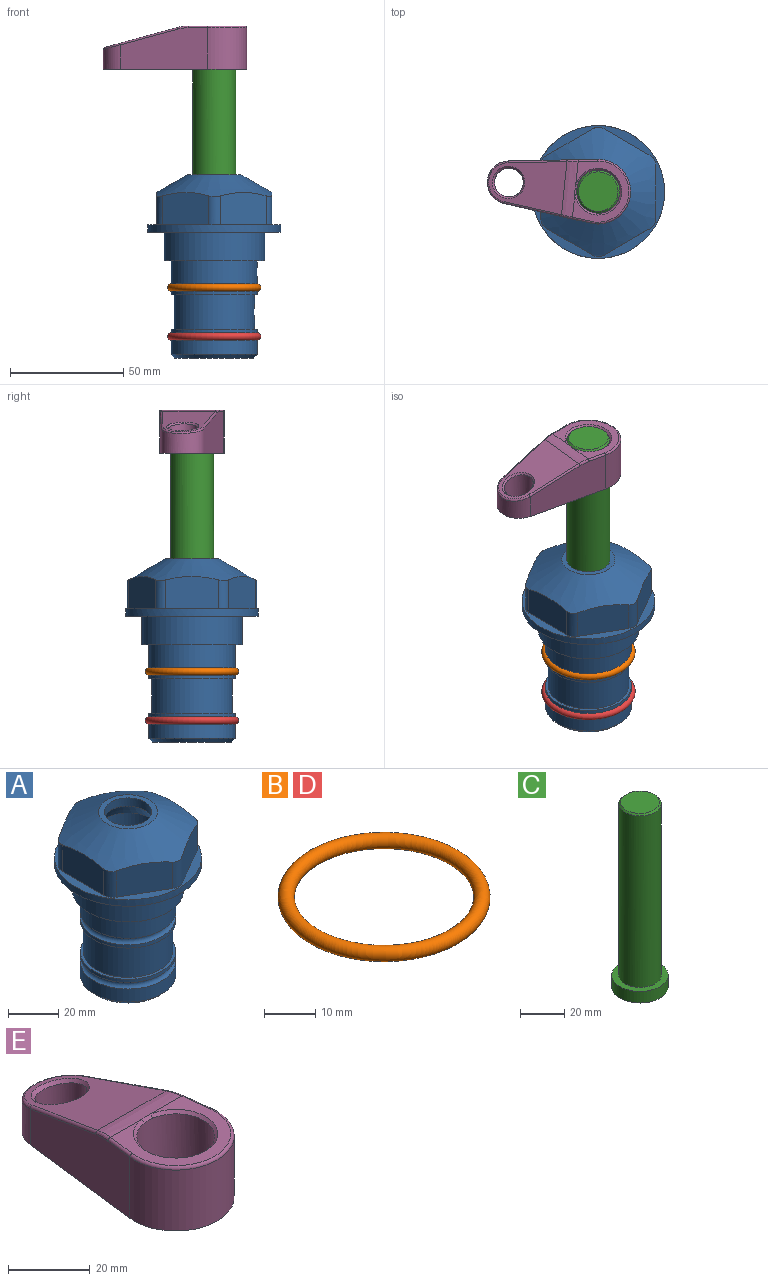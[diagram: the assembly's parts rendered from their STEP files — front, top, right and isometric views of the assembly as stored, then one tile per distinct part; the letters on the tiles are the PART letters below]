
ASSEMBLY  parts=5 mates=4
PART A: 36 faces, bbox 58.7x58.7x81 mm
  f0: cylinder r=17.78mm len=35.56mm, axis (0,0,1), area 1670.8mm2, adj f23,f24,f31
  f1: cylinder r=19.05mm len=38.1mm, axis (0,0,1), area 1191.9mm2, adj f26,f27,f30
  f2: plane 58.66x58.66mm, normal (0,0,-1), area 1150.6mm2, adj f3,f28
  f3: cylinder r=29.33mm len=58.66mm, axis (0,0,-1), area 585.1mm2, adj f2,f4
  f4: plane 58.66x58.66mm, normal (0,0,1), area 475.9mm2, adj f3,f5,f6,f7,f8,f9,f10,f11
  f5: plane 20.32x14.34mm, normal (-0.5,0.87,0), area 324.4mm2, adj f4,f15,f16,f17
  f6: plane 20.32x14.34mm, normal (0.5,0.87,0), area 324.4mm2, adj f4,f14,f15,f17
  f7: plane 23.48x14.34mm, normal (1,0,0), area 324.4mm2, adj f4,f13,f14,f17
  f8: plane 20.32x14.34mm, normal (0.5,-0.87,0), area 324.4mm2, adj f4,f12,f13,f17
  f9: plane 20.32x14.34mm, normal (-0.5,-0.87,0), area 324.4mm2, adj f4,f11,f12,f17
  f10: plane 23.48x14.34mm, normal (-1,0,0), area 324.4mm2, adj f4,f11,f16,f17
  f11: cylinder r=5.08mm len=12.85mm, axis (0,0,-1), area 67.2mm2, adj f4,f9,f10,f17
  f12: cylinder r=5.08mm len=12.85mm, axis (0,0,-1), area 67.2mm2, adj f4,f8,f9,f17
  f13: cylinder r=5.08mm len=12.85mm, axis (0,0,-1), area 67.2mm2, adj f4,f7,f8,f17
  f14: cylinder r=5.08mm len=12.85mm, axis (0,0,-1), area 67.2mm2, adj f4,f6,f7,f17
  f15: cylinder r=5.08mm len=12.85mm, axis (0,0,-1), area 67.2mm2, adj f4,f5,f6,f17
  f16: cylinder r=5.08mm len=12.85mm, axis (0,0,-1), area 67.2mm2, adj f4,f5,f10,f17
  f17: cone r=11.73mm half-angle=60deg, axis (0,0,-1), area 2071.8mm2, adj f5,f6,f7,f8,f9,f10,f11,f12
  f18: plane 23.46x23.46mm, normal (0,0,1), area 147.4mm2, adj f17,f35
  f19: plane 34.93x34.93mm, normal (0,0,-1), area 958mm2, adj f29
  f20: cylinder r=19.05mm len=38.1mm, axis (0,0,1), area 760.1mm2, adj f21,f29
  f21: torus R=19.05mm, axis (0,0,1), area 565.3mm2, adj f20,f22
  f22: cylinder r=19.05mm len=38.1mm, axis (0,0,1), area 190mm2, adj f21,f23
  f23: plane 38.1x38.1mm, normal (0,0,1), area 146.9mm2, adj f0,f22
  f24: plane 38.1x38.1mm, normal (0,0,-1), area 146.9mm2, adj f0,f25
  f25: cylinder r=19.05mm len=38.1mm, axis (0,0,1), area 190mm2, adj f24,f26
  f26: torus R=19.05mm, axis (0,0,1), area 565.3mm2, adj f1,f25
  f27: plane 44.45x44.45mm, normal (0,0,-1), area 411.7mm2, adj f1,f28
  f28: cylinder r=22.23mm len=44.45mm, axis (0,0,1), area 1773.5mm2, adj f2,f27
  f29: cone r=19.05mm half-angle=45deg, axis (0,0,1), area 257.5mm2, adj f19,f20
  f30: cylinder r=3.17mm len=6.75mm, axis (-1,0,0), area 128mm2, adj f1,f33
  f31: cylinder r=3.17mm len=6.35mm, axis (-1,0,0), area 102.5mm2, adj f0,f33
  f32: plane 25.4x25.4mm, normal (0,0,1), area 506.7mm2, adj f33
  f33: cylinder r=12.7mm len=66.42mm, axis (0,0,-1), area 5236.2mm2, adj f30,f31,f32,f34
  f34: cone r=9.53mm half-angle=30deg, axis (0,0,-1), area 443.4mm2, adj f33,f35
  f35: cylinder r=9.53mm len=19.05mm, axis (0,0,-1), area 240.9mm2, adj f18,f34
PART B: 1 faces, bbox 44.7x44.7x3.2 mm
  f0: torus R=19.05mm, axis (0,0,1), area 1193.9mm2
PART C: 6 faces, bbox 25.4x25.4x101.6 mm
  f0: plane 17.46x17.46mm, normal (0,0,1), area 239.5mm2, adj f5
  f1: plane 25.4x25.4mm, normal (0,0,-1), area 506.7mm2, adj f2
  f2: cylinder r=12.7mm len=25.4mm, axis (0,0,1), area 506.7mm2, adj f1,f3
  f3: plane 25.4x25.4mm, normal (0,0,1), area 221.7mm2, adj f2,f4
  f4: cylinder r=9.53mm len=94.46mm, axis (0,0,1), area 5653mm2, adj f3,f5
  f5: cone r=8.73mm half-angle=45deg, axis (0,0,-1), area 64.4mm2, adj f0,f4
PART D: same geometry as B
PART E: 31 faces, bbox 31.7x65.5x19.8 mm
  f0: plane 39.12x18.26mm, normal (0.99,0.12,0), area 612.2mm2, adj f1,f4,f7,f11,f13,f15
  f1: cylinder r=9.53mm len=18.91mm, axis (0,0,-1), area 296.1mm2, adj f0,f2,f7,f17
  f2: plane 39.12x18.26mm, normal (-0.99,0.12,0), area 612.2mm2, adj f1,f4,f7,f12,f14,f16
  f3: cylinder r=6.35mm len=12.7mm, axis (0,0,-1), area 362.4mm2, adj f7,f18
  f4: cylinder r=14.29mm len=28.58mm, axis (0,0,-1), area 882.2mm2, adj f0,f2,f7,f10
  f5: cylinder r=9.53mm len=19.05mm, axis (0,0,-1), area 1092.6mm2, adj f7,f19,f20
  f6: plane 26.99x23.69mm, normal (0,0,1), area 216.2mm2, adj f9,f10,f11,f12,f19
  f7: plane 63.5x28.58mm, normal (0,0,-1), area 661.8mm2, adj f0,f1,f2,f3,f4,f5,f22,f23
  f8: plane 33.52x23.6mm, normal (0,0.26,0.97), area 486mm2, adj f9,f15,f16,f17,f18
  f9: cylinder r=19.05mm len=24.72mm, axis (1,0,0), area 120.4mm2, adj f6,f8,f13,f14,f20
  f10: torus R=13.49mm, axis (0,0,1), area 59mm2, adj f4,f6,f11,f12
  f11: cylinder r=0.79mm len=8.67mm, axis (0.12,-0.99,0), area 10.8mm2, adj f0,f6,f10,f13
  f12: cylinder r=0.79mm len=8.67mm, axis (0.12,0.99,0), area 10.8mm2, adj f2,f6,f10,f14
  f13: bspline ~4.95x1.42mm, area 6.1mm2, adj f0,f9,f11,f15
  f14: bspline ~4.95x1.42mm, area 6.1mm2, adj f2,f9,f12,f16
  f15: cylinder r=0.79mm len=25.95mm, axis (0.12,-0.96,0.26), area 32.9mm2, adj f0,f8,f13,f17
  f16: cylinder r=0.79mm len=25.95mm, axis (0.12,0.96,-0.26), area 32.9mm2, adj f2,f8,f14,f17
  f17: bspline ~18.91x8.38mm, area 30mm2, adj f1,f8,f15,f16
  f18: bspline ~14.29x14.29mm, area 48.3mm2, adj f3,f8
  f19: cone r=9.53mm half-angle=45deg, axis (0,0,1), area 66.5mm2, adj f5,f6,f20
  f20: bspline ~3.22x0.96mm, area 3.5mm2, adj f5,f9,f19
  f21: plane 2.75x2.72mm, normal (0,0,-1), area 2.9mm2, adj f23,f25,f28
  f22: plane 23.05x15.88mm, normal (-0.99,-0.12,0), area 323.6mm2, adj f7,f25,f26,f27,f28,f29
  f23: plane 23.05x15.88mm, normal (0.99,-0.12,0), area 323.6mm2, adj f7,f21,f25,f27,f28,f30
  f24: cylinder r=9.53mm len=10.69mm, axis (0,0,-1), area 114.7mm2, adj f7,f27,f29,f30
  f25: cylinder r=12.7mm len=20.59mm, axis (0,0,-1), area 381.1mm2, adj f7,f21,f22,f23,f26,f28
  f26: plane 2.75x2.72mm, normal (0,0,-1), area 2.9mm2, adj f22,f25,f28
  f27: plane 19.72x18.37mm, normal (0,-0.26,-0.97), area 291.8mm2, adj f22,f23,f24,f28,f29,f30
  f28: cylinder r=15.88mm len=19.92mm, axis (1,0,0), area 54.8mm2, adj f21,f22,f23,f25,f26,f27
  f29: cylinder r=1.59mm len=11mm, axis (0,0,-1), area 34.7mm2, adj f7,f22,f24,f27
  f30: cylinder r=1.59mm len=11mm, axis (0,0,-1), area 34.7mm2, adj f7,f23,f24,f27
PLACE A at identity fixed
PLACE B at identity
PLACE C rot(axis=(0,0,1),84.2deg) t=(0,0,27.55)mm
PLACE D t=(0,0,-21.59)mm
PLACE E rot(axis=(0,0,1),84.2deg) t=(0,0,27.55)mm
MATE fastened A.f0 <-> D.f0  axis (0,0,1) through (0,0,-46.1)mm
MATE fastened A.f0 <-> B.f0  axis (0,0,1) through (0,0,-24.51)mm
MATE cylindrical A.f0 <-> C.f2  axis (0,0,1) through (0,0,-50.55)mm
MATE fastened E.f4 <-> C.f2  axis (0,0,1) through (0,0,91.05)mm
